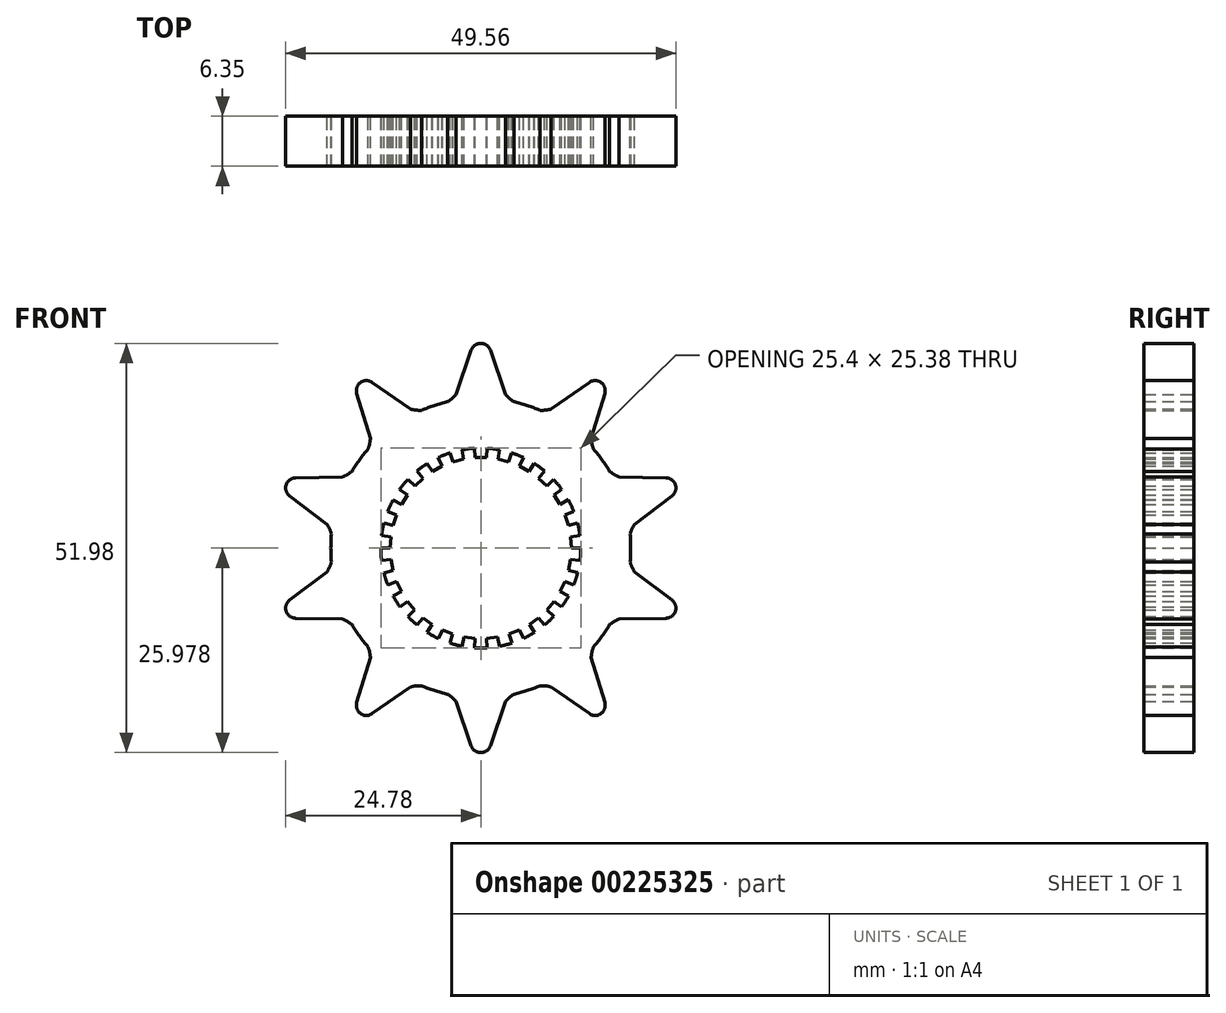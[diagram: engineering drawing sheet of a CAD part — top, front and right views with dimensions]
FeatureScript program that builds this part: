
annotation { "Feature Type Name" : "Feature", "Feature Type Description" : "" }
export const myFeature = defineFeature(function(context is Context, id is Id, definition is map)
    precondition{}
    {
        {
            var Q0;
            Q0=qCreatedBy(makeId("Front.planeOp"),FACE);
            var sketch = newSketch(context, id + "F0", { "sketchPlane" : qUnion([Q0])});
            skLineSegment(sketch, "E0.0.0", {"start": v(11.14, -6.1) * mm, "end": v(10.1, -5.53) * mm});
            skLineSegment(sketch, "E0.0.1", {"start": v(10.1, -5.53) * mm, "end": v(10.7, -4.25) * mm});
            skLineSegment(sketch, "E0.0.2", {"start": v(10.7, -4.25) * mm, "end": v(11.8, -4.68) * mm});
            skLineSegment(sketch, "E0.0.4", {"start": v(12.3, -3.14) * mm, "end": v(11.15, -2.85) * mm});
            skLineSegment(sketch, "E0.0.5", {"start": v(11.15, -2.85) * mm, "end": v(11.42, -1.45) * mm});
            skLineSegment(sketch, "E0.0.6", {"start": v(11.42, -1.45) * mm, "end": v(12.6, -1.6) * mm});
            skLineSegment(sketch, "E0.0.8", {"start": v(12.7, 0.02) * mm, "end": v(11.5, 0.01) * mm});
            skLineSegment(sketch, "E0.0.9", {"start": v(11.5, 0.01) * mm, "end": v(11.42, 1.43) * mm});
            skLineSegment(sketch, "E0.0.10", {"start": v(11.42, 1.43) * mm, "end": v(12.6, 1.59) * mm});
            skLineSegment(sketch, "E0.0.12", {"start": v(12.3, 3.18) * mm, "end": v(11.14, 2.87) * mm});
            skLineSegment(sketch, "E0.0.13", {"start": v(11.14, 2.87) * mm, "end": v(10.7, 4.23) * mm});
            skLineSegment(sketch, "E0.0.14", {"start": v(10.7, 4.23) * mm, "end": v(11.8, 4.67) * mm});
            skLineSegment(sketch, "E0.0.16", {"start": v(11.12, 6.14) * mm, "end": v(10.08, 5.55) * mm});
            skLineSegment(sketch, "E0.0.17", {"start": v(10.08, 5.55) * mm, "end": v(9.32, 6.76) * mm});
            skLineSegment(sketch, "E0.0.18", {"start": v(9.32, 6.76) * mm, "end": v(10.28, 7.46) * mm});
            skLineSegment(sketch, "E0.0.20", {"start": v(9.24, 8.7) * mm, "end": v(8.38, 7.89) * mm});
            skLineSegment(sketch, "E0.0.21", {"start": v(8.38, 7.89) * mm, "end": v(7.35, 8.86) * mm});
            skLineSegment(sketch, "E0.0.22", {"start": v(7.35, 8.86) * mm, "end": v(8.1, 9.78) * mm});
            skLineSegment(sketch, "E0.0.24", {"start": v(6.79, 10.73) * mm, "end": v(6.16, 9.72) * mm});
            skLineSegment(sketch, "E0.0.25", {"start": v(6.16, 9.72) * mm, "end": v(4.91, 10.4) * mm});
            skLineSegment(sketch, "E0.0.26", {"start": v(4.91, 10.4) * mm, "end": v(5.41, 11.49) * mm});
            skLineSegment(sketch, "E0.0.28", {"start": v(3.9, 12.09) * mm, "end": v(3.55, 10.95) * mm});
            skLineSegment(sketch, "E0.0.29", {"start": v(3.55, 10.95) * mm, "end": v(2.17, 11.3) * mm});
            skLineSegment(sketch, "E0.0.30", {"start": v(2.17, 11.3) * mm, "end": v(2.38, 12.47) * mm});
            skLineSegment(sketch, "E0.0.32", {"start": v(0.78, 12.68) * mm, "end": v(0.71, 11.49) * mm});
            skLineSegment(sketch, "E0.0.33", {"start": v(0.71, 11.49) * mm, "end": v(-0.71, 11.49) * mm});
            skLineSegment(sketch, "E0.0.34", {"start": v(-0.71, 11.49) * mm, "end": v(-0.8, 12.68) * mm});
            skLineSegment(sketch, "E0.0.36", {"start": v(-2.4, 12.47) * mm, "end": v(-2.17, 11.3) * mm});
            skLineSegment(sketch, "E0.0.37", {"start": v(-2.17, 11.3) * mm, "end": v(-3.55, 10.95) * mm});
            skLineSegment(sketch, "E0.0.38", {"start": v(-3.55, 10.95) * mm, "end": v(-3.92, 12.08) * mm});
            skLineSegment(sketch, "E0.0.40", {"start": v(-5.43, 11.48) * mm, "end": v(-4.91, 10.4) * mm});
            skLineSegment(sketch, "E0.0.41", {"start": v(-4.91, 10.4) * mm, "end": v(-6.16, 9.72) * mm});
            skLineSegment(sketch, "E0.0.42", {"start": v(-6.16, 9.72) * mm, "end": v(-6.8, 10.72) * mm});
            skLineSegment(sketch, "E0.0.44", {"start": v(-8.11, 9.77) * mm, "end": v(-7.35, 8.86) * mm});
            skLineSegment(sketch, "E0.0.45", {"start": v(-7.35, 8.86) * mm, "end": v(-8.38, 7.89) * mm});
            skLineSegment(sketch, "E0.0.46", {"start": v(-8.38, 7.89) * mm, "end": v(-9.26, 8.7) * mm});
            skLineSegment(sketch, "E0.0.48", {"start": v(-10.29, 7.45) * mm, "end": v(-9.32, 6.76) * mm});
            skLineSegment(sketch, "E0.0.49", {"start": v(-9.32, 6.76) * mm, "end": v(-10.08, 5.55) * mm});
            skLineSegment(sketch, "E0.0.50", {"start": v(-10.08, 5.55) * mm, "end": v(-11.13, 6.12) * mm});
            skLineSegment(sketch, "E0.0.52", {"start": v(-11.82, 4.66) * mm, "end": v(-10.7, 4.23) * mm});
            skLineSegment(sketch, "E0.0.53", {"start": v(-10.7, 4.23) * mm, "end": v(-11.14, 2.87) * mm});
            skLineSegment(sketch, "E0.0.54", {"start": v(-11.14, 2.87) * mm, "end": v(-12.3, 3.16) * mm});
            skLineSegment(sketch, "E0.0.56", {"start": v(-12.6, 1.57) * mm, "end": v(-11.42, 1.43) * mm});
            skLineSegment(sketch, "E0.0.57", {"start": v(-11.42, 1.43) * mm, "end": v(-11.5, 0.01) * mm});
            skLineSegment(sketch, "E0.0.58", {"start": v(-11.5, 0.01) * mm, "end": v(-12.7, 0) * mm});
            skLineSegment(sketch, "E0.0.60", {"start": v(-12.6, -1.61) * mm, "end": v(-11.42, -1.45) * mm});
            skLineSegment(sketch, "E0.0.61", {"start": v(-11.42, -1.45) * mm, "end": v(-11.15, -2.85) * mm});
            skLineSegment(sketch, "E0.0.62", {"start": v(-11.15, -2.85) * mm, "end": v(-12.3, -3.15) * mm});
            skLineSegment(sketch, "E0.0.64", {"start": v(-11.8, -4.7) * mm, "end": v(-10.7, -4.25) * mm});
            skLineSegment(sketch, "E0.0.65", {"start": v(-10.7, -4.25) * mm, "end": v(-10.1, -5.53) * mm});
            skLineSegment(sketch, "E0.0.66", {"start": v(-10.1, -5.53) * mm, "end": v(-11.13, -6.12) * mm});
            skLineSegment(sketch, "E0.0.68", {"start": v(-10.26, -7.48) * mm, "end": v(-9.3, -6.77) * mm});
            skLineSegment(sketch, "E0.0.69", {"start": v(-9.3, -6.77) * mm, "end": v(-8.4, -7.87) * mm});
            skLineSegment(sketch, "E0.0.70", {"start": v(-8.4, -7.87) * mm, "end": v(-9.26, -8.7) * mm});
            skLineSegment(sketch, "E0.0.72", {"start": v(-8.08, -9.8) * mm, "end": v(-7.33, -8.88) * mm});
            skLineSegment(sketch, "E0.0.73", {"start": v(-7.33, -8.88) * mm, "end": v(-6.18, -9.71) * mm});
            skLineSegment(sketch, "E0.0.74", {"start": v(-6.18, -9.71) * mm, "end": v(-6.8, -10.72) * mm});
            skLineSegment(sketch, "E0.0.76", {"start": v(-5.39, -11.5) * mm, "end": v(-4.9, -10.42) * mm});
            skLineSegment(sketch, "E0.0.77", {"start": v(-4.9, -10.42) * mm, "end": v(-3.57, -10.94) * mm});
            skLineSegment(sketch, "E0.0.78", {"start": v(-3.57, -10.94) * mm, "end": v(-3.93, -12.08) * mm});
            skLineSegment(sketch, "E0.0.80", {"start": v(-2.36, -12.48) * mm, "end": v(-2.15, -11.3) * mm});
            skLineSegment(sketch, "E0.0.81", {"start": v(-2.15, -11.3) * mm, "end": v(-0.73, -11.49) * mm});
            skLineSegment(sketch, "E0.0.82", {"start": v(-0.73, -11.49) * mm, "end": v(-0.8, -12.67) * mm});
            skLineSegment(sketch, "E0.0.84", {"start": v(0.82, -12.67) * mm, "end": v(0.73, -11.49) * mm});
            skLineSegment(sketch, "E0.0.85", {"start": v(0.73, -11.49) * mm, "end": v(2.15, -11.3) * mm});
            skLineSegment(sketch, "E0.0.86", {"start": v(2.15, -11.3) * mm, "end": v(2.38, -12.48) * mm});
            skLineSegment(sketch, "E0.0.88", {"start": v(3.95, -12.07) * mm, "end": v(3.57, -10.94) * mm});
            skLineSegment(sketch, "E0.0.89", {"start": v(3.57, -10.94) * mm, "end": v(4.9, -10.42) * mm});
            skLineSegment(sketch, "E0.0.90", {"start": v(4.9, -10.42) * mm, "end": v(5.4, -11.5) * mm});
            skLineSegment(sketch, "E0.0.92", {"start": v(6.82, -10.71) * mm, "end": v(6.18, -9.71) * mm});
            skLineSegment(sketch, "E0.0.93", {"start": v(6.18, -9.71) * mm, "end": v(7.33, -8.88) * mm});
            skLineSegment(sketch, "E0.0.94", {"start": v(7.33, -8.88) * mm, "end": v(8.1, -9.79) * mm});
            skLineSegment(sketch, "E0.0.96", {"start": v(9.27, -8.68) * mm, "end": v(8.4, -7.87) * mm});
            skLineSegment(sketch, "E0.0.97", {"start": v(8.4, -7.87) * mm, "end": v(9.3, -6.77) * mm});
            skLineSegment(sketch, "E0.0.98", {"start": v(9.3, -6.77) * mm, "end": v(10.27, -7.47) * mm});
            skCircle(sketch, "E1", {"center": v(0, 0) * mm, "radius": 19.05 * mm});
            skArc(sketch, "E2", {"start": v(-6.8, 10.72) * mm, "mid": v(-7.47, 10.27) * mm, "end": v(-8.11, 9.77) * mm});
            skArc(sketch, "E3.trimOffspring", {"start": v(-3.92, 12.08) * mm, "mid": v(-4.68, 11.8) * mm, "end": v(-5.43, 11.48) * mm});
            skArc(sketch, "E4.trimOffspring", {"start": v(-0.8, 12.68) * mm, "mid": v(-1.6, 12.6) * mm, "end": v(-2.4, 12.47) * mm});
            skArc(sketch, "E5.trimOffspring", {"start": v(2.38, 12.47) * mm, "mid": v(1.58, 12.6) * mm, "end": v(0.78, 12.68) * mm});
            skArc(sketch, "E6.trimOffspring", {"start": v(5.41, 11.49) * mm, "mid": v(4.67, 11.81) * mm, "end": v(3.9, 12.09) * mm});
            skArc(sketch, "E7.trimOffspring", {"start": v(8.1, 9.78) * mm, "mid": v(7.46, 10.28) * mm, "end": v(6.79, 10.73) * mm});
            skArc(sketch, "E8.trimOffspring", {"start": v(10.28, 7.46) * mm, "mid": v(9.78, 8.1) * mm, "end": v(9.24, 8.7) * mm});
            skArc(sketch, "E9.trimOffspring", {"start": v(11.8, 4.67) * mm, "mid": v(11.49, 5.42) * mm, "end": v(11.12, 6.14) * mm});
            skArc(sketch, "E10.trimOffspring", {"start": v(12.6, 1.59) * mm, "mid": v(12.47, 2.39) * mm, "end": v(12.3, 3.18) * mm});
            skArc(sketch, "E11.trimOffspring", {"start": v(12.6, -1.6) * mm, "mid": v(12.68, -0.79) * mm, "end": v(12.7, 0.02) * mm});
            skArc(sketch, "E12.trimOffspring", {"start": v(11.8, -4.68) * mm, "mid": v(12.08, -3.92) * mm, "end": v(12.3, -3.14) * mm});
            skArc(sketch, "E13.trimOffspring", {"start": v(10.27, -7.47) * mm, "mid": v(10.73, -6.8) * mm, "end": v(11.14, -6.1) * mm});
            skArc(sketch, "E14.trimOffspring", {"start": v(8.1, -9.79) * mm, "mid": v(8.7, -9.25) * mm, "end": v(9.27, -8.68) * mm});
            skArc(sketch, "E15.trimOffspring", {"start": v(5.4, -11.5) * mm, "mid": v(6.13, -11.12) * mm, "end": v(6.82, -10.71) * mm});
            skArc(sketch, "E16.trimOffspring", {"start": v(2.38, -12.48) * mm, "mid": v(3.17, -12.3) * mm, "end": v(3.95, -12.07) * mm});
            skArc(sketch, "E17.trimOffspring", {"start": v(-0.8, -12.67) * mm, "mid": v(0, -12.7) * mm, "end": v(0.82, -12.67) * mm});
            skArc(sketch, "E18.trimOffspring", {"start": v(-3.93, -12.08) * mm, "mid": v(-3.15, -12.3) * mm, "end": v(-2.36, -12.48) * mm});
            skArc(sketch, "E19.trimOffspring", {"start": v(-6.8, -10.72) * mm, "mid": v(-6.11, -11.13) * mm, "end": v(-5.39, -11.5) * mm});
            skArc(sketch, "E20.trimOffspring", {"start": v(-9.26, -8.7) * mm, "mid": v(-8.69, -9.26) * mm, "end": v(-8.08, -9.8) * mm});
            skArc(sketch, "E21.trimOffspring", {"start": v(-11.13, -6.12) * mm, "mid": v(-10.72, -6.81) * mm, "end": v(-10.26, -7.48) * mm});
            skArc(sketch, "E22.trimOffspring", {"start": v(-12.3, -3.15) * mm, "mid": v(-12.08, -3.93) * mm, "end": v(-11.8, -4.7) * mm});
            skArc(sketch, "E23.trimOffspring", {"start": v(-12.7, 0) * mm, "mid": v(-12.67, -0.8) * mm, "end": v(-12.6, -1.61) * mm});
            skArc(sketch, "E24.trimOffspring", {"start": v(-12.3, 3.16) * mm, "mid": v(-12.48, 2.37) * mm, "end": v(-12.6, 1.57) * mm});
            skArc(sketch, "E25.trimOffspring", {"start": v(-11.13, 6.12) * mm, "mid": v(-11.5, 5.4) * mm, "end": v(-11.82, 4.66) * mm});
            skArc(sketch, "E26.trimOffspring", {"start": v(-9.26, 8.7) * mm, "mid": v(-9.8, 8.09) * mm, "end": v(-10.29, 7.45) * mm});
            skLineSegment(sketch, "E27", {"start": v(-3.17, 19.5) * mm, "end": v(-1.2, 25.13) * mm});
            skArc(sketch, "E28", {"start": v(1.2, 25.13) * mm, "mid": v(0, 26) * mm, "end": v(-1.2, 25.13) * mm});
            skLineSegment(sketch, "E29.MirrorCS", {"start": v(3.17, 19.5) * mm, "end": v(1.2, 25.13) * mm});
            skLineSegment(sketch, "E30.9.0", {"start": v(8.4, 17.08) * mm, "end": v(8.42, 17.09) * mm});
            skPoint(sketch, "E30.center", {"position": v(-0.07, -0.31) * mm});
            skArc(sketch, "E31", {"start": v(-4.2, 18.58) * mm, "mid": v(-3.65, 19) * mm, "end": v(-3.17, 19.5) * mm});
            skPoint(sketch, "E32.orphan", {"position": v(-3.43, 18.74) * mm});
            skArc(sketch, "E33.MirrorCS", {"start": v(4.2, 18.58) * mm, "mid": v(3.65, 19) * mm, "end": v(3.17, 19.5) * mm});
            skPoint(sketch, "E34", {"position": v(0, 26) * mm});
            skPoint(sketch, "E35", {"position": v(-0.14, -26.62) * mm});
            skLineSegment(sketch, "E36", {"start": v(0, 26) * mm, "end": v(-0.14, -26.62) * mm});
            skPoint(sketch, "E37.orphan", {"position": v(-15.95, 19.6) * mm});
            skPoint(sketch, "E38.orphan", {"position": v(-14.03, 13.91) * mm});
            skPoint(sketch, "E39.orphan", {"position": v(-1.35, -25.76) * mm});
            skPoint(sketch, "E40.orphan", {"position": v(13.97, 20.94) * mm});
            skPoint(sketch, "E41.orphan", {"position": v(15.92, 19.52) * mm});
            skPoint(sketch, "E42.orphan", {"position": v(14.03, 13.91) * mm});
            skPoint(sketch, "E43.orphan", {"position": v(3.43, 18.74) * mm});
            skLineSegment(sketch, "E44.1.0", {"start": v(-14.03, 13.91) * mm, "end": v(-15.75, 19.62) * mm});
            skArc(sketch, "E44.1.1", {"start": v(-13.8, 21.04) * mm, "mid": v(-15.28, 21.03) * mm, "end": v(-15.75, 19.62) * mm});
            skLineSegment(sketch, "E44.1.2", {"start": v(-8.9, 17.64) * mm, "end": v(-13.8, 21.04) * mm});
            skArc(sketch, "E44.1.3", {"start": v(-7.53, 17.5) * mm, "mid": v(-8.22, 17.52) * mm, "end": v(-8.9, 17.64) * mm});
            skArc(sketch, "E44.1.4", {"start": v(-14.32, 12.57) * mm, "mid": v(-14.12, 13.23) * mm, "end": v(-14.03, 13.91) * mm});
            skLineSegment(sketch, "E44.2.0", {"start": v(-19.52, 3.01) * mm, "end": v(-24.28, 6.62) * mm});
            skArc(sketch, "E44.2.1", {"start": v(-23.53, 8.92) * mm, "mid": v(-24.72, 8.03) * mm, "end": v(-24.28, 6.62) * mm});
            skLineSegment(sketch, "E44.2.2", {"start": v(-17.57, 9.04) * mm, "end": v(-23.53, 8.92) * mm});
            skArc(sketch, "E44.2.3", {"start": v(-16.38, 9.73) * mm, "mid": v(-16.94, 9.34) * mm, "end": v(-17.57, 9.04) * mm});
            skArc(sketch, "E44.2.4", {"start": v(-18.97, 1.75) * mm, "mid": v(-19.2, 2.4) * mm, "end": v(-19.52, 3.01) * mm});
            skLineSegment(sketch, "E44.3.0", {"start": v(-17.57, -9.04) * mm, "end": v(-23.53, -8.92) * mm});
            skArc(sketch, "E44.3.1", {"start": v(-24.28, -6.62) * mm, "mid": v(-24.72, -8.03) * mm, "end": v(-23.53, -8.92) * mm});
            skLineSegment(sketch, "E44.3.2", {"start": v(-19.52, -3.01) * mm, "end": v(-24.28, -6.62) * mm});
            skArc(sketch, "E44.3.3", {"start": v(-18.97, -1.75) * mm, "mid": v(-19.2, -2.4) * mm, "end": v(-19.52, -3.01) * mm});
            skArc(sketch, "E44.3.4", {"start": v(-16.38, -9.73) * mm, "mid": v(-16.94, -9.34) * mm, "end": v(-17.57, -9.04) * mm});
            skLineSegment(sketch, "E44.4.0", {"start": v(-8.9, -17.64) * mm, "end": v(-13.8, -21.04) * mm});
            skArc(sketch, "E44.4.1", {"start": v(-15.75, -19.62) * mm, "mid": v(-15.28, -21.03) * mm, "end": v(-13.8, -21.04) * mm});
            skLineSegment(sketch, "E44.4.2", {"start": v(-14.03, -13.91) * mm, "end": v(-15.75, -19.62) * mm});
            skArc(sketch, "E44.4.3", {"start": v(-14.32, -12.57) * mm, "mid": v(-14.12, -13.23) * mm, "end": v(-14.03, -13.91) * mm});
            skArc(sketch, "E44.4.4", {"start": v(-7.53, -17.5) * mm, "mid": v(-8.22, -17.52) * mm, "end": v(-8.9, -17.64) * mm});
            skLineSegment(sketch, "E44.5.0", {"start": v(3.17, -19.5) * mm, "end": v(1.2, -25.13) * mm});
            skArc(sketch, "E44.5.1", {"start": v(-1.2, -25.13) * mm, "mid": v(0, -26) * mm, "end": v(1.2, -25.13) * mm});
            skLineSegment(sketch, "E44.5.2", {"start": v(-3.17, -19.5) * mm, "end": v(-1.2, -25.13) * mm});
            skArc(sketch, "E44.5.3", {"start": v(-4.2, -18.58) * mm, "mid": v(-3.65, -19) * mm, "end": v(-3.17, -19.5) * mm});
            skArc(sketch, "E44.5.4", {"start": v(4.2, -18.58) * mm, "mid": v(3.65, -19) * mm, "end": v(3.17, -19.5) * mm});
            skLineSegment(sketch, "E44.6.0", {"start": v(14.03, -13.91) * mm, "end": v(15.75, -19.62) * mm});
            skArc(sketch, "E44.6.1", {"start": v(13.8, -21.04) * mm, "mid": v(15.28, -21.03) * mm, "end": v(15.75, -19.62) * mm});
            skLineSegment(sketch, "E44.6.2", {"start": v(8.9, -17.64) * mm, "end": v(13.8, -21.04) * mm});
            skArc(sketch, "E44.6.3", {"start": v(7.53, -17.5) * mm, "mid": v(8.22, -17.52) * mm, "end": v(8.9, -17.64) * mm});
            skArc(sketch, "E44.6.4", {"start": v(14.32, -12.57) * mm, "mid": v(14.12, -13.23) * mm, "end": v(14.03, -13.91) * mm});
            skLineSegment(sketch, "E44.7.0", {"start": v(19.52, -3.01) * mm, "end": v(24.28, -6.62) * mm});
            skArc(sketch, "E44.7.1", {"start": v(23.53, -8.92) * mm, "mid": v(24.72, -8.03) * mm, "end": v(24.28, -6.62) * mm});
            skLineSegment(sketch, "E44.7.2", {"start": v(17.57, -9.04) * mm, "end": v(23.53, -8.92) * mm});
            skArc(sketch, "E44.7.3", {"start": v(16.38, -9.73) * mm, "mid": v(16.94, -9.34) * mm, "end": v(17.57, -9.04) * mm});
            skArc(sketch, "E44.7.4", {"start": v(18.97, -1.75) * mm, "mid": v(19.2, -2.4) * mm, "end": v(19.52, -3.01) * mm});
            skLineSegment(sketch, "E44.8.0", {"start": v(17.57, 9.04) * mm, "end": v(23.53, 8.92) * mm});
            skArc(sketch, "E44.8.1", {"start": v(24.28, 6.62) * mm, "mid": v(24.72, 8.03) * mm, "end": v(23.53, 8.92) * mm});
            skLineSegment(sketch, "E44.8.2", {"start": v(19.52, 3.01) * mm, "end": v(24.28, 6.62) * mm});
            skArc(sketch, "E44.8.3", {"start": v(18.97, 1.75) * mm, "mid": v(19.2, 2.4) * mm, "end": v(19.52, 3.01) * mm});
            skArc(sketch, "E44.8.4", {"start": v(16.38, 9.73) * mm, "mid": v(16.94, 9.34) * mm, "end": v(17.57, 9.04) * mm});
            skLineSegment(sketch, "E44.9.0", {"start": v(8.9, 17.64) * mm, "end": v(13.8, 21.04) * mm});
            skArc(sketch, "E44.9.1", {"start": v(15.75, 19.62) * mm, "mid": v(15.28, 21.03) * mm, "end": v(13.8, 21.04) * mm});
            skLineSegment(sketch, "E44.9.2", {"start": v(14.03, 13.91) * mm, "end": v(15.75, 19.62) * mm});
            skArc(sketch, "E44.9.3", {"start": v(14.32, 12.57) * mm, "mid": v(14.12, 13.23) * mm, "end": v(14.03, 13.91) * mm});
            skArc(sketch, "E44.9.4", {"start": v(7.53, 17.5) * mm, "mid": v(8.22, 17.52) * mm, "end": v(8.9, 17.64) * mm});
            skSolve(sketch);
        }
        {
            var Q0;
            Q0 = qSketchRegion(id + "F0", true);
            extrude(context, id + "F1", {"entities" : qUnion([Q0]), "depth" : 6.35 * mm});
        }
    });
